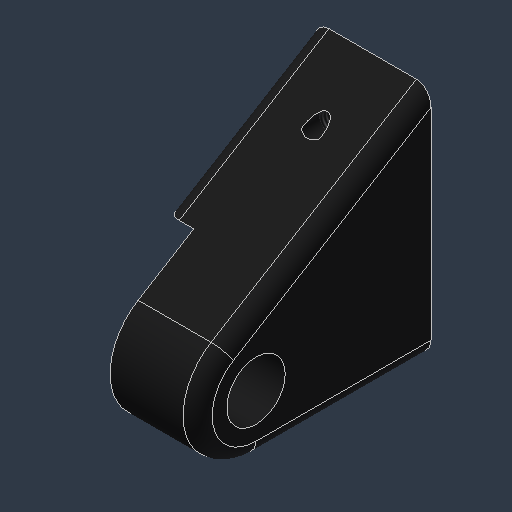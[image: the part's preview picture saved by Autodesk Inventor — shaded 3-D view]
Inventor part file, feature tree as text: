
AUTODESK INVENTOR PART (.ipt)
format: ipt  version: 2024.3 (Build 283343000, 343)  size: 171,520 bytes
history: native  units: mm (DEFAULTED — no unit token found)
features: sketch x4, extrude x2, hole x2, pattern_linear x1, fillet x1, projected_geometry x1
ambient origin geometry x8: Origin, YZ Plane, XZ Plane, XY Plane, X Axis, Y Axis, Z Axis, Center Point
bodies: Solid1 (feature_tree)
feature tree (11):
  extrude  "Extrusion1"  Depth=12.7mm
  hole  "Hole1"  [1 undecoded]
  extrude  "Extrusion2"  Depth=6.35mm TaperAngle=0.0deg
  hole  "Hole2"  [1 undecoded]
  pattern_linear  "Rectangular Pattern1"  Count1=4 Spacing1=12.7mm
  fillet  "Fillet1"  Radius=3.175mm
  sketch  "Sketch2"  dims[d0=12.7mm d1=50.8mm]
  sketch  "Sketch3"  dims[d2=38.1mm d3=25.4mm d4=0.0mm]
  sketch  "Sketch4"  dims[d5=38.1mm d6=6.35mm d7=0.0mm]
  sketch  "Sketch5"  dims[d8=12.7mm d9=19.05mm d10=9.779mm d11=1.9558mm d12=14.3117mm d13=25.4mm d14=20.594885mm d15=7.9375mm d16=3.9624mm d17=9.652mm d18=9.779mm d19=6.35mm d20=14.3117mm d21=13.6144mm d22=20.594885mm d23=40.0mm d25=12.7mm d26=3.175mm]
  projected_geometry  "Projected Loop1"
note: 2 required parameter values undecoded (feature->parameter linkage not recoverable at this tier; creation-order binding heuristic only, values carry confidence <= 0.55)
